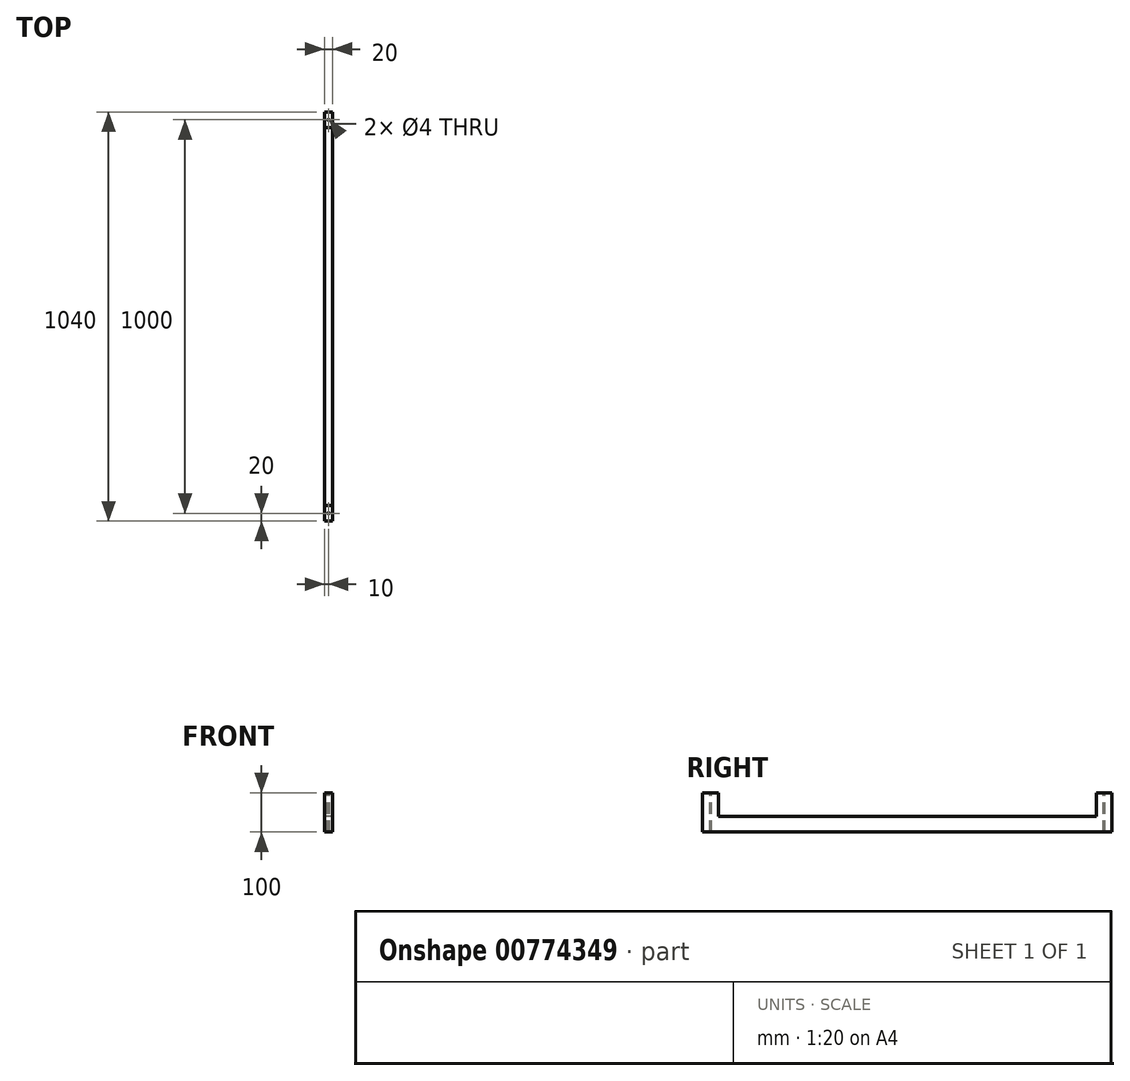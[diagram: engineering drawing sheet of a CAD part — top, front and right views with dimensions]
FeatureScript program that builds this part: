
annotation { "Feature Type Name" : "Feature", "Feature Type Description" : "" }
export const myFeature = defineFeature(function(context is Context, id is Id, definition is map)
    precondition{}
    {
        {
            var Q0;
            Q0=qCreatedBy(makeId("Right.planeOp"),FACE);
            var sketch = newSketch(context, id + "F0", { "sketchPlane" : qUnion([Q0])});
            skLineSegment(sketch, "E0", {"start": v(-500, 80) * mm, "end": v(-500, 0) * mm});
            skLineSegment(sketch, "E1", {"start": v(-500, 0) * mm, "end": v(500, 0) * mm});
            skLineSegment(sketch, "E2", {"start": v(500, 0) * mm, "end": v(500, 80) * mm});
            skSolve(sketch);
        }
        {
            var Q0;
            Q0=sQuery(id+"F0.wireOp",VERTEX,"E0.start");
            var Q1;
            Q1=qCreatedBy(makeId("Top.planeOp"),FACE);
            cPlane(context, id + "F1", {"entities" : qUnion([Q0, Q1]), "cplaneType" : CPlaneType.PLANE_POINT, "offset" : 25 * mm, "width" : 150 * mm, "height" : 150 * mm});
        }
        {
            var Q0;
            Q0=qCreatedBy(id+"F1.planeOp",FACE);
            var sketch = newSketch(context, id + "F2", { "sketchPlane" : qUnion([Q0])});
            skLineSegment(sketch, "E3.bottom", {"start": v(10, -520) * mm, "end": v(-10, -520) * mm});
            skLineSegment(sketch, "E3.top", {"start": v(10, -480) * mm, "end": v(-10, -480) * mm});
            skLineSegment(sketch, "E3.left", {"start": v(10, -520) * mm, "end": v(10, -480) * mm});
            skLineSegment(sketch, "E3.right", {"start": v(-10, -520) * mm, "end": v(-10, -480) * mm});
            skPoint(sketch, "E3.middle", {"position": v(0, -500) * mm});
            skSolve(sketch);
        }
        {
            var Q0;
            Q0=makeQuery(id+"F2.imprint","IMPRINT",FACE,{"disambiguationData":[TD([[makeQuery(id+"F2.imprint","IMPRINT",EDGE,{"derivedFrom":sQuery(id+"F2.wireOp",EDGE,"E3.bottom")}),-1.0]])]});
            var Q1;
            Q1=sQuery(id+"F0.wireOp",EDGE,"E0");
            var Q2;
            Q2=sQuery(id+"F0.wireOp",EDGE,"E1");
            var Q3;
            Q3=sQuery(id+"F0.wireOp",EDGE,"E2");
            sweep(context, id + "F3", {"profiles" : qUnion([Q0]), "path" : qUnion([Q1, Q2, Q3])});
        }
        {
            var Q0;
            Q0=makeQuery(id+"F3.opSweep","CAP_FACE",FACE,{"disambiguationData":[OSD([sQuery(id+"F0.wireOp",VERTEX,"E0.start"),sQuery(id+"F2.wireOp",EDGE,"E3.bottom"),sQuery(id+"F2.wireOp",EDGE,"E3.top"),sQuery(id+"F2.wireOp",EDGE,"E3.left"),sQuery(id+"F2.wireOp",EDGE,"E3.right")])],"isStart":true});
            var sketch = newSketch(context, id + "F4", { "sketchPlane" : qUnion([Q0])});
            skPoint(sketch, "E4", {"position": v(0, -500) * mm});
            skPoint(sketch, "E4.positionSnap0", {"position": v(0, -480) * mm});
            skPoint(sketch, "E4.positionSnap1", {"position": v(-10, -500) * mm});
            skSolve(sketch);
        }
        {
            var Q0;
            Q0=makeQuery(id+"F3.opSweep","CAP_FACE",FACE,{"disambiguationData":[OSD([sQuery(id+"F0.wireOp",VERTEX,"E2.end"),sQuery(id+"F2.wireOp",EDGE,"E3.bottom"),sQuery(id+"F2.wireOp",EDGE,"E3.top"),sQuery(id+"F2.wireOp",EDGE,"E3.left"),sQuery(id+"F2.wireOp",EDGE,"E3.right")])],"isStart":false});
            var sketch = newSketch(context, id + "F5", { "sketchPlane" : qUnion([Q0])});
            skPoint(sketch, "E5", {"position": v(0, 500) * mm});
            skPoint(sketch, "E5.positionSnap0", {"position": v(-10, 500) * mm});
            skSolve(sketch);
        }
        {
            var Q0;
            Q0=sQuery(id+"F4.wireOp",VERTEX,"E4");
            var Q1;
            Q1=sQuery(id+"F5.wireOp",VERTEX,"E5");
            var Q2;
            Q2=makeQuery(id+"F3.opSweep","SWEPT_BODY",BODY,{"disambiguationData":[OSD([sQuery(id+"F0.wireOp",EDGE,"E2"),sQuery(id+"F2.wireOp",EDGE,"E3.bottom"),sQuery(id+"F2.wireOp",EDGE,"E3.top"),sQuery(id+"F2.wireOp",EDGE,"E3.left"),sQuery(id+"F2.wireOp",EDGE,"E3.right")])]});
            hole(context, id + "F6", {"style" : HoleStyle.SIMPLE, "endStyle" : HoleEndStyle.BLIND, "holeDiameter" : 4 * mm, "majorDiameter" : 5 * mm, "holeDepth" : 100 * mm, "isTappedThrough" : true, "tappedDepth" : 12 * mm, "tapClearance" : 3, "startFromSketch" : true, "locations" : qUnion([Q0, Q1]), "scope" : qUnion([Q2])});
        }
    });
